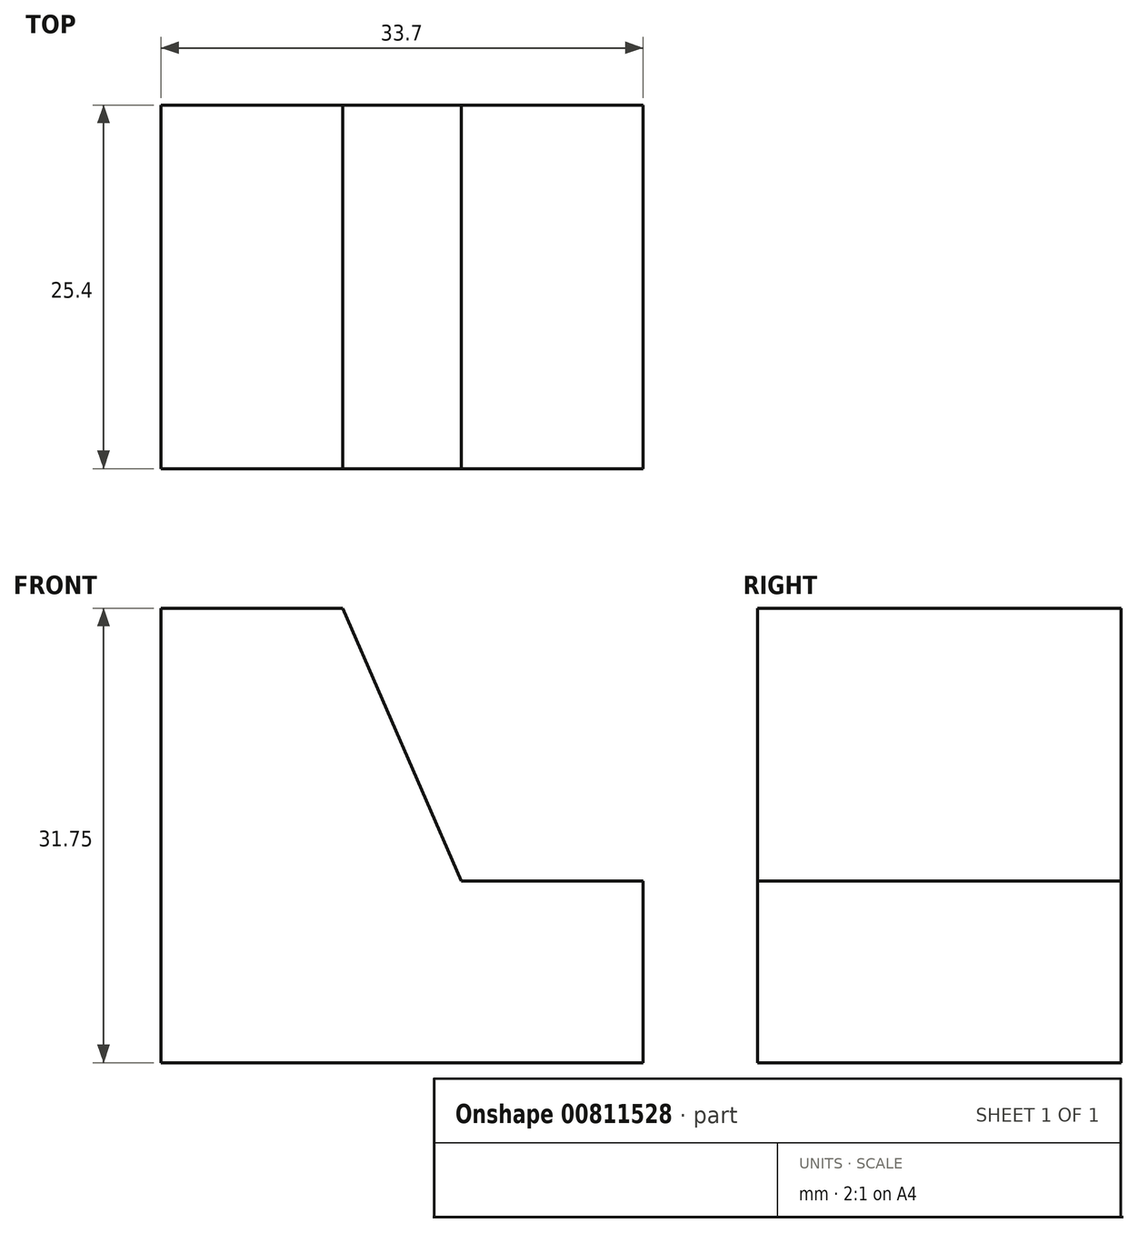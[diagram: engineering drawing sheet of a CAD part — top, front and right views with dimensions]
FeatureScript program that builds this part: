
annotation { "Feature Type Name" : "Feature", "Feature Type Description" : "" }
export const myFeature = defineFeature(function(context is Context, id is Id, definition is map)
    precondition{}
    {
        {
            var Q0;
            Q0=qCreatedBy(makeId("Front.planeOp"),FACE);
            var sketch = newSketch(context, id + "F0", { "sketchPlane" : qUnion([Q0])});
            skLineSegment(sketch, "E0", {"start": v(0, 0) * mm, "end": v(0, 31.75) * mm});
            skLineSegment(sketch, "E1", {"start": v(0, 31.75) * mm, "end": v(12.7, 31.75) * mm});
            skLineSegment(sketch, "E2", {"start": v(-4.4, 0) * mm, "end": v(33.7, 0) * mm});
            skLineSegment(sketch, "E3", {"start": v(33.7, 0) * mm, "end": v(33.7, 12.7) * mm});
            skLineSegment(sketch, "E4", {"start": v(33.7, 12.7) * mm, "end": v(21, 12.7) * mm});
            skLineSegment(sketch, "E5", {"start": v(21, 12.7) * mm, "end": v(12.7, 31.75) * mm});
            skSolve(sketch);
        }
        {
            var Q0;
            Q0 = qSketchRegion(id + "F0", true);
            extrude(context, id + "F1", {"entities" : qUnion([Q0]), "depth" : 25.4 * mm, "offsetDistance" : 25.4 * mm});
        }
    });
